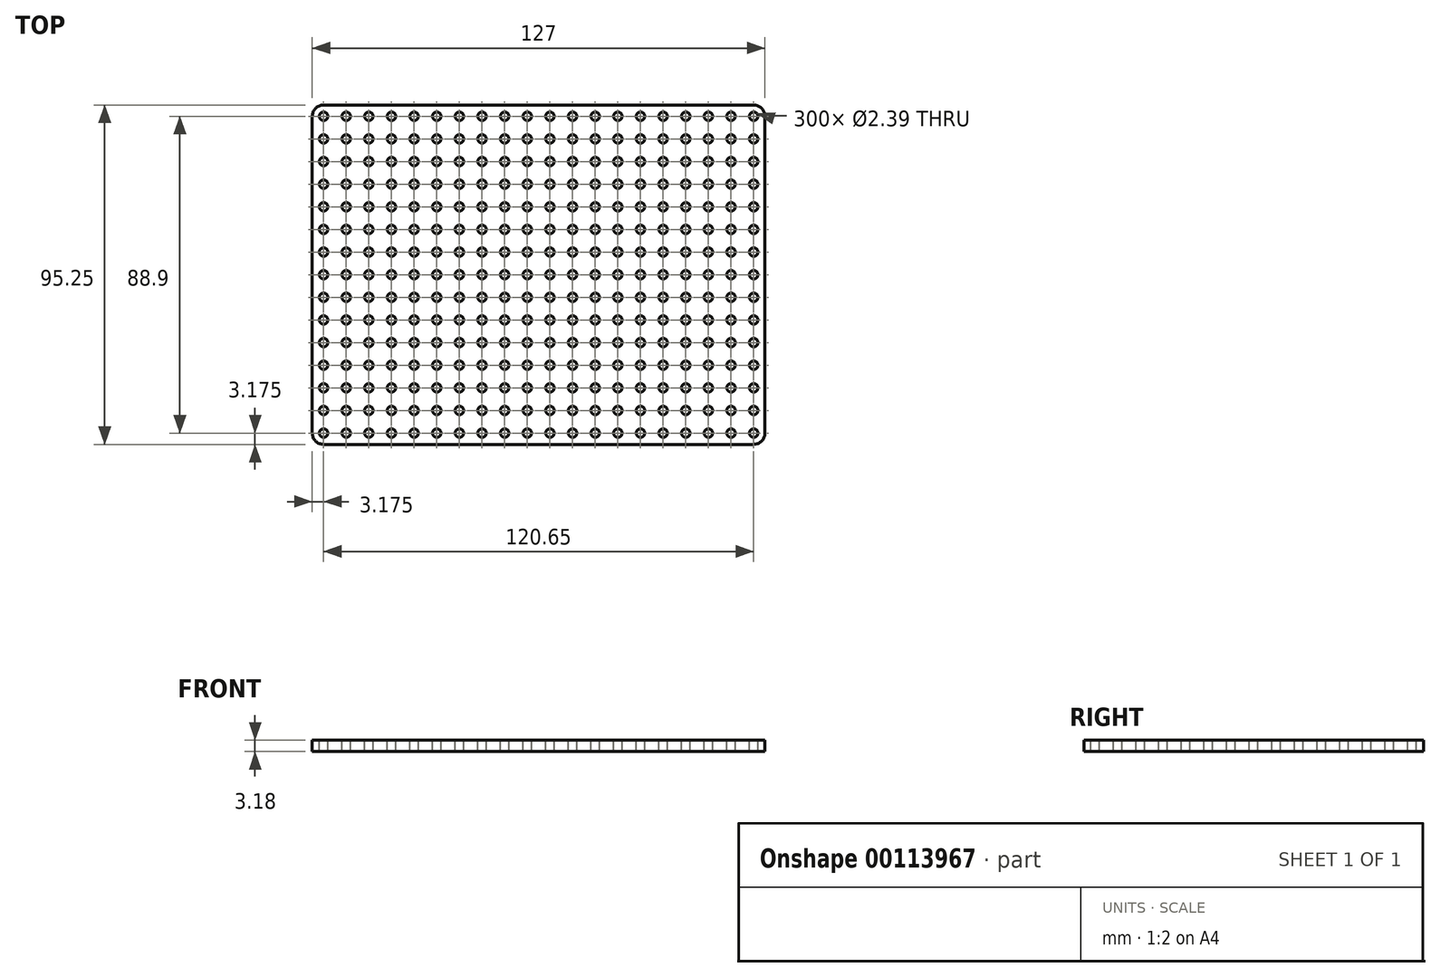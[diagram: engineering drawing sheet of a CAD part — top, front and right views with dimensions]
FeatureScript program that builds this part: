
annotation { "Feature Type Name" : "Feature", "Feature Type Description" : "" }
export const myFeature = defineFeature(function(context is Context, id is Id, definition is map)
    precondition{}
    {
        {
            var Q0;
            Q0=qCreatedBy(makeId("Top.planeOp"),FACE);
            var sketch = newSketch(context, id + "F0", { "sketchPlane" : qUnion([Q0])});
            skLineSegment(sketch, "E0.bottom", {"start": v(3.17, 0) * mm, "end": v(123.83, 0) * mm});
            skLineSegment(sketch, "E0.top", {"start": v(3.17, 95.25) * mm, "end": v(123.82, 95.25) * mm});
            skLineSegment(sketch, "E0.left", {"start": v(0, 3.17) * mm, "end": v(0, 92.08) * mm});
            skLineSegment(sketch, "E0.right", {"start": v(127, 3.17) * mm, "end": v(127, 92.08) * mm});
            skPoint(sketch, "E1.visualSharp", {"position": v(0, 95.25) * mm});
            skArc(sketch, "E1.filletArc", {"start": v(3.17, 95.25) * mm, "mid": v(0.93, 94.32) * mm, "end": v(0, 92.08) * mm});
            skPoint(sketch, "E2.visualSharp", {"position": v(127, 95.25) * mm});
            skArc(sketch, "E2.filletArc", {"start": v(127, 92.08) * mm, "mid": v(126.07, 94.32) * mm, "end": v(123.82, 95.25) * mm});
            skPoint(sketch, "E3.visualSharp", {"position": v(127, 0) * mm});
            skArc(sketch, "E3.filletArc", {"start": v(123.83, 0) * mm, "mid": v(126.07, 0.93) * mm, "end": v(127, 3.18) * mm});
            skPoint(sketch, "E4.visualSharp", {"position": v(0, 0) * mm});
            skArc(sketch, "E4.filletArc", {"start": v(0, 3.17) * mm, "mid": v(0.93, 0.93) * mm, "end": v(3.17, 0) * mm});
            skSolve(sketch);
        }
        {
            var Q0;
            Q0=qSketchRegion(id+"F0",true);
            extrude(context, id + "F1", {"entities" : qUnion([Q0]), "depth" : 3.17 * mm});
        }
        {
            var Q0;
            Q0=makeQuery(id+"F1.opExtrude","CAP_FACE",FACE,{"disambiguationData":[OSD([sQuery(id+"F0.wireOp",EDGE,"E0.bottom"),sQuery(id+"F0.wireOp",EDGE,"E0.top"),sQuery(id+"F0.wireOp",EDGE,"E0.left"),sQuery(id+"F0.wireOp",EDGE,"E0.right"),sQuery(id+"F0.wireOp",EDGE,"E1.filletArc"),sQuery(id+"F0.wireOp",EDGE,"E2.filletArc"),sQuery(id+"F0.wireOp",EDGE,"E3.filletArc"),sQuery(id+"F0.wireOp",EDGE,"E4.filletArc")])],"isStart":false});
            var sketch = newSketch(context, id + "F2", { "sketchPlane" : qUnion([Q0])});
            skCircle(sketch, "E5", {"center": v(3.18, 3.17) * mm, "radius": 1.2 * mm});
            skCircle(sketch, "E6.0.1.0", {"center": v(3.18, 9.52) * mm, "radius": 1.2 * mm});
            skCircle(sketch, "E6.0.2.0", {"center": v(3.18, 15.88) * mm, "radius": 1.2 * mm});
            skCircle(sketch, "E6.0.3.0", {"center": v(3.18, 22.23) * mm, "radius": 1.2 * mm});
            skCircle(sketch, "E6.0.4.0", {"center": v(3.18, 28.58) * mm, "radius": 1.2 * mm});
            skCircle(sketch, "E6.0.5.0", {"center": v(3.18, 34.93) * mm, "radius": 1.2 * mm});
            skCircle(sketch, "E6.0.6.0", {"center": v(3.18, 41.28) * mm, "radius": 1.2 * mm});
            skCircle(sketch, "E6.0.7.0", {"center": v(3.18, 47.63) * mm, "radius": 1.2 * mm});
            skCircle(sketch, "E6.0.8.0", {"center": v(3.18, 53.98) * mm, "radius": 1.2 * mm});
            skCircle(sketch, "E6.0.9.0", {"center": v(3.18, 60.33) * mm, "radius": 1.2 * mm});
            skCircle(sketch, "E6.0.10.0", {"center": v(3.18, 66.68) * mm, "radius": 1.2 * mm});
            skCircle(sketch, "E6.0.11.0", {"center": v(3.18, 73.03) * mm, "radius": 1.2 * mm});
            skCircle(sketch, "E6.0.12.0", {"center": v(3.18, 79.38) * mm, "radius": 1.2 * mm});
            skCircle(sketch, "E6.0.13.0", {"center": v(3.18, 85.73) * mm, "radius": 1.2 * mm});
            skCircle(sketch, "E6.0.14.0", {"center": v(3.18, 92.08) * mm, "radius": 1.2 * mm});
            skCircle(sketch, "E6.1.0.0", {"center": v(9.53, 3.17) * mm, "radius": 1.2 * mm});
            skCircle(sketch, "E6.1.1.0", {"center": v(9.53, 9.52) * mm, "radius": 1.2 * mm});
            skCircle(sketch, "E6.1.2.0", {"center": v(9.53, 15.88) * mm, "radius": 1.2 * mm});
            skCircle(sketch, "E6.1.3.0", {"center": v(9.53, 22.23) * mm, "radius": 1.2 * mm});
            skCircle(sketch, "E6.1.4.0", {"center": v(9.53, 28.58) * mm, "radius": 1.2 * mm});
            skCircle(sketch, "E6.1.5.0", {"center": v(9.53, 34.93) * mm, "radius": 1.2 * mm});
            skCircle(sketch, "E6.1.6.0", {"center": v(9.53, 41.28) * mm, "radius": 1.2 * mm});
            skCircle(sketch, "E6.1.7.0", {"center": v(9.53, 47.63) * mm, "radius": 1.2 * mm});
            skCircle(sketch, "E6.1.8.0", {"center": v(9.53, 53.98) * mm, "radius": 1.2 * mm});
            skCircle(sketch, "E6.1.9.0", {"center": v(9.53, 60.33) * mm, "radius": 1.2 * mm});
            skCircle(sketch, "E6.1.10.0", {"center": v(9.53, 66.68) * mm, "radius": 1.2 * mm});
            skCircle(sketch, "E6.1.11.0", {"center": v(9.53, 73.03) * mm, "radius": 1.2 * mm});
            skCircle(sketch, "E6.1.12.0", {"center": v(9.53, 79.38) * mm, "radius": 1.2 * mm});
            skCircle(sketch, "E6.1.13.0", {"center": v(9.53, 85.73) * mm, "radius": 1.2 * mm});
            skCircle(sketch, "E6.1.14.0", {"center": v(9.53, 92.08) * mm, "radius": 1.2 * mm});
            skCircle(sketch, "E6.2.0.0", {"center": v(15.88, 3.17) * mm, "radius": 1.2 * mm});
            skCircle(sketch, "E6.2.1.0", {"center": v(15.88, 9.52) * mm, "radius": 1.2 * mm});
            skCircle(sketch, "E6.2.2.0", {"center": v(15.88, 15.88) * mm, "radius": 1.2 * mm});
            skCircle(sketch, "E6.2.3.0", {"center": v(15.88, 22.23) * mm, "radius": 1.2 * mm});
            skCircle(sketch, "E6.2.4.0", {"center": v(15.88, 28.58) * mm, "radius": 1.2 * mm});
            skCircle(sketch, "E6.2.5.0", {"center": v(15.88, 34.93) * mm, "radius": 1.2 * mm});
            skCircle(sketch, "E6.2.6.0", {"center": v(15.88, 41.28) * mm, "radius": 1.2 * mm});
            skCircle(sketch, "E6.2.7.0", {"center": v(15.88, 47.63) * mm, "radius": 1.2 * mm});
            skCircle(sketch, "E6.2.8.0", {"center": v(15.88, 53.98) * mm, "radius": 1.2 * mm});
            skCircle(sketch, "E6.2.9.0", {"center": v(15.88, 60.33) * mm, "radius": 1.2 * mm});
            skCircle(sketch, "E6.2.10.0", {"center": v(15.88, 66.68) * mm, "radius": 1.2 * mm});
            skCircle(sketch, "E6.2.11.0", {"center": v(15.88, 73.03) * mm, "radius": 1.2 * mm});
            skCircle(sketch, "E6.2.12.0", {"center": v(15.88, 79.38) * mm, "radius": 1.2 * mm});
            skCircle(sketch, "E6.2.13.0", {"center": v(15.88, 85.73) * mm, "radius": 1.2 * mm});
            skCircle(sketch, "E6.2.14.0", {"center": v(15.88, 92.08) * mm, "radius": 1.2 * mm});
            skCircle(sketch, "E6.3.0.0", {"center": v(22.22, 3.17) * mm, "radius": 1.2 * mm});
            skCircle(sketch, "E6.3.1.0", {"center": v(22.22, 9.52) * mm, "radius": 1.2 * mm});
            skCircle(sketch, "E6.3.2.0", {"center": v(22.22, 15.88) * mm, "radius": 1.2 * mm});
            skCircle(sketch, "E6.3.3.0", {"center": v(22.22, 22.23) * mm, "radius": 1.2 * mm});
            skCircle(sketch, "E6.3.4.0", {"center": v(22.22, 28.58) * mm, "radius": 1.2 * mm});
            skCircle(sketch, "E6.3.5.0", {"center": v(22.22, 34.93) * mm, "radius": 1.2 * mm});
            skCircle(sketch, "E6.3.6.0", {"center": v(22.22, 41.28) * mm, "radius": 1.2 * mm});
            skCircle(sketch, "E6.3.7.0", {"center": v(22.22, 47.63) * mm, "radius": 1.2 * mm});
            skCircle(sketch, "E6.3.8.0", {"center": v(22.22, 53.98) * mm, "radius": 1.2 * mm});
            skCircle(sketch, "E6.3.9.0", {"center": v(22.22, 60.33) * mm, "radius": 1.2 * mm});
            skCircle(sketch, "E6.3.10.0", {"center": v(22.22, 66.68) * mm, "radius": 1.2 * mm});
            skCircle(sketch, "E6.3.11.0", {"center": v(22.22, 73.03) * mm, "radius": 1.2 * mm});
            skCircle(sketch, "E6.3.12.0", {"center": v(22.22, 79.38) * mm, "radius": 1.2 * mm});
            skCircle(sketch, "E6.3.13.0", {"center": v(22.22, 85.73) * mm, "radius": 1.2 * mm});
            skCircle(sketch, "E6.3.14.0", {"center": v(22.22, 92.08) * mm, "radius": 1.2 * mm});
            skCircle(sketch, "E6.4.0.0", {"center": v(28.57, 3.17) * mm, "radius": 1.2 * mm});
            skCircle(sketch, "E6.4.1.0", {"center": v(28.57, 9.52) * mm, "radius": 1.2 * mm});
            skCircle(sketch, "E6.4.2.0", {"center": v(28.57, 15.88) * mm, "radius": 1.2 * mm});
            skCircle(sketch, "E6.4.3.0", {"center": v(28.57, 22.23) * mm, "radius": 1.2 * mm});
            skCircle(sketch, "E6.4.4.0", {"center": v(28.57, 28.58) * mm, "radius": 1.2 * mm});
            skCircle(sketch, "E6.4.5.0", {"center": v(28.57, 34.93) * mm, "radius": 1.2 * mm});
            skCircle(sketch, "E6.4.6.0", {"center": v(28.57, 41.28) * mm, "radius": 1.2 * mm});
            skCircle(sketch, "E6.4.7.0", {"center": v(28.57, 47.63) * mm, "radius": 1.2 * mm});
            skCircle(sketch, "E6.4.8.0", {"center": v(28.57, 53.98) * mm, "radius": 1.2 * mm});
            skCircle(sketch, "E6.4.9.0", {"center": v(28.57, 60.33) * mm, "radius": 1.2 * mm});
            skCircle(sketch, "E6.4.10.0", {"center": v(28.57, 66.68) * mm, "radius": 1.2 * mm});
            skCircle(sketch, "E6.4.11.0", {"center": v(28.57, 73.03) * mm, "radius": 1.2 * mm});
            skCircle(sketch, "E6.4.12.0", {"center": v(28.57, 79.38) * mm, "radius": 1.2 * mm});
            skCircle(sketch, "E6.4.13.0", {"center": v(28.57, 85.73) * mm, "radius": 1.2 * mm});
            skCircle(sketch, "E6.4.14.0", {"center": v(28.57, 92.08) * mm, "radius": 1.2 * mm});
            skCircle(sketch, "E6.5.0.0", {"center": v(34.92, 3.17) * mm, "radius": 1.2 * mm});
            skCircle(sketch, "E6.5.1.0", {"center": v(34.92, 9.52) * mm, "radius": 1.2 * mm});
            skCircle(sketch, "E6.5.2.0", {"center": v(34.92, 15.88) * mm, "radius": 1.2 * mm});
            skCircle(sketch, "E6.5.3.0", {"center": v(34.92, 22.23) * mm, "radius": 1.2 * mm});
            skCircle(sketch, "E6.5.4.0", {"center": v(34.92, 28.58) * mm, "radius": 1.2 * mm});
            skCircle(sketch, "E6.5.5.0", {"center": v(34.92, 34.93) * mm, "radius": 1.2 * mm});
            skCircle(sketch, "E6.5.6.0", {"center": v(34.92, 41.28) * mm, "radius": 1.2 * mm});
            skCircle(sketch, "E6.5.7.0", {"center": v(34.92, 47.63) * mm, "radius": 1.2 * mm});
            skCircle(sketch, "E6.5.8.0", {"center": v(34.92, 53.98) * mm, "radius": 1.2 * mm});
            skCircle(sketch, "E6.5.9.0", {"center": v(34.92, 60.33) * mm, "radius": 1.2 * mm});
            skCircle(sketch, "E6.5.10.0", {"center": v(34.92, 66.68) * mm, "radius": 1.2 * mm});
            skCircle(sketch, "E6.5.11.0", {"center": v(34.92, 73.03) * mm, "radius": 1.2 * mm});
            skCircle(sketch, "E6.5.12.0", {"center": v(34.92, 79.38) * mm, "radius": 1.2 * mm});
            skCircle(sketch, "E6.5.13.0", {"center": v(34.92, 85.73) * mm, "radius": 1.2 * mm});
            skCircle(sketch, "E6.5.14.0", {"center": v(34.92, 92.08) * mm, "radius": 1.2 * mm});
            skCircle(sketch, "E6.6.0.0", {"center": v(41.27, 3.17) * mm, "radius": 1.2 * mm});
            skCircle(sketch, "E6.6.1.0", {"center": v(41.27, 9.52) * mm, "radius": 1.2 * mm});
            skCircle(sketch, "E6.6.2.0", {"center": v(41.27, 15.88) * mm, "radius": 1.2 * mm});
            skCircle(sketch, "E6.6.3.0", {"center": v(41.27, 22.23) * mm, "radius": 1.2 * mm});
            skCircle(sketch, "E6.6.4.0", {"center": v(41.27, 28.58) * mm, "radius": 1.2 * mm});
            skCircle(sketch, "E6.6.5.0", {"center": v(41.27, 34.93) * mm, "radius": 1.2 * mm});
            skCircle(sketch, "E6.6.6.0", {"center": v(41.27, 41.28) * mm, "radius": 1.2 * mm});
            skCircle(sketch, "E6.6.7.0", {"center": v(41.27, 47.63) * mm, "radius": 1.2 * mm});
            skCircle(sketch, "E6.6.8.0", {"center": v(41.27, 53.98) * mm, "radius": 1.2 * mm});
            skCircle(sketch, "E6.6.9.0", {"center": v(41.27, 60.33) * mm, "radius": 1.2 * mm});
            skCircle(sketch, "E6.6.10.0", {"center": v(41.27, 66.68) * mm, "radius": 1.2 * mm});
            skCircle(sketch, "E6.6.11.0", {"center": v(41.27, 73.03) * mm, "radius": 1.2 * mm});
            skCircle(sketch, "E6.6.12.0", {"center": v(41.27, 79.38) * mm, "radius": 1.2 * mm});
            skCircle(sketch, "E6.6.13.0", {"center": v(41.27, 85.73) * mm, "radius": 1.2 * mm});
            skCircle(sketch, "E6.6.14.0", {"center": v(41.27, 92.08) * mm, "radius": 1.2 * mm});
            skCircle(sketch, "E6.7.0.0", {"center": v(47.62, 3.17) * mm, "radius": 1.2 * mm});
            skCircle(sketch, "E6.7.1.0", {"center": v(47.62, 9.52) * mm, "radius": 1.2 * mm});
            skCircle(sketch, "E6.7.2.0", {"center": v(47.62, 15.88) * mm, "radius": 1.2 * mm});
            skCircle(sketch, "E6.7.3.0", {"center": v(47.62, 22.23) * mm, "radius": 1.2 * mm});
            skCircle(sketch, "E6.7.4.0", {"center": v(47.62, 28.58) * mm, "radius": 1.2 * mm});
            skCircle(sketch, "E6.7.5.0", {"center": v(47.62, 34.93) * mm, "radius": 1.2 * mm});
            skCircle(sketch, "E6.7.6.0", {"center": v(47.62, 41.28) * mm, "radius": 1.2 * mm});
            skCircle(sketch, "E6.7.7.0", {"center": v(47.62, 47.63) * mm, "radius": 1.2 * mm});
            skCircle(sketch, "E6.7.8.0", {"center": v(47.62, 53.98) * mm, "radius": 1.2 * mm});
            skCircle(sketch, "E6.7.9.0", {"center": v(47.62, 60.33) * mm, "radius": 1.2 * mm});
            skCircle(sketch, "E6.7.10.0", {"center": v(47.62, 66.68) * mm, "radius": 1.2 * mm});
            skCircle(sketch, "E6.7.11.0", {"center": v(47.62, 73.03) * mm, "radius": 1.2 * mm});
            skCircle(sketch, "E6.7.12.0", {"center": v(47.62, 79.38) * mm, "radius": 1.2 * mm});
            skCircle(sketch, "E6.7.13.0", {"center": v(47.62, 85.73) * mm, "radius": 1.2 * mm});
            skCircle(sketch, "E6.7.14.0", {"center": v(47.62, 92.08) * mm, "radius": 1.2 * mm});
            skCircle(sketch, "E6.8.0.0", {"center": v(53.97, 3.17) * mm, "radius": 1.2 * mm});
            skCircle(sketch, "E6.8.1.0", {"center": v(53.97, 9.52) * mm, "radius": 1.2 * mm});
            skCircle(sketch, "E6.8.2.0", {"center": v(53.97, 15.88) * mm, "radius": 1.2 * mm});
            skCircle(sketch, "E6.8.3.0", {"center": v(53.97, 22.23) * mm, "radius": 1.2 * mm});
            skCircle(sketch, "E6.8.4.0", {"center": v(53.97, 28.58) * mm, "radius": 1.2 * mm});
            skCircle(sketch, "E6.8.5.0", {"center": v(53.97, 34.93) * mm, "radius": 1.2 * mm});
            skCircle(sketch, "E6.8.6.0", {"center": v(53.97, 41.28) * mm, "radius": 1.2 * mm});
            skCircle(sketch, "E6.8.7.0", {"center": v(53.97, 47.63) * mm, "radius": 1.2 * mm});
            skCircle(sketch, "E6.8.8.0", {"center": v(53.97, 53.98) * mm, "radius": 1.2 * mm});
            skCircle(sketch, "E6.8.9.0", {"center": v(53.97, 60.33) * mm, "radius": 1.2 * mm});
            skCircle(sketch, "E6.8.10.0", {"center": v(53.97, 66.68) * mm, "radius": 1.2 * mm});
            skCircle(sketch, "E6.8.11.0", {"center": v(53.97, 73.03) * mm, "radius": 1.2 * mm});
            skCircle(sketch, "E6.8.12.0", {"center": v(53.97, 79.38) * mm, "radius": 1.2 * mm});
            skCircle(sketch, "E6.8.13.0", {"center": v(53.97, 85.73) * mm, "radius": 1.2 * mm});
            skCircle(sketch, "E6.8.14.0", {"center": v(53.97, 92.08) * mm, "radius": 1.2 * mm});
            skCircle(sketch, "E6.9.0.0", {"center": v(60.32, 3.17) * mm, "radius": 1.2 * mm});
            skCircle(sketch, "E6.9.1.0", {"center": v(60.32, 9.52) * mm, "radius": 1.2 * mm});
            skCircle(sketch, "E6.9.2.0", {"center": v(60.32, 15.88) * mm, "radius": 1.2 * mm});
            skCircle(sketch, "E6.9.3.0", {"center": v(60.32, 22.23) * mm, "radius": 1.2 * mm});
            skCircle(sketch, "E6.9.4.0", {"center": v(60.32, 28.58) * mm, "radius": 1.2 * mm});
            skCircle(sketch, "E6.9.5.0", {"center": v(60.32, 34.93) * mm, "radius": 1.2 * mm});
            skCircle(sketch, "E6.9.6.0", {"center": v(60.32, 41.28) * mm, "radius": 1.2 * mm});
            skCircle(sketch, "E6.9.7.0", {"center": v(60.32, 47.63) * mm, "radius": 1.2 * mm});
            skCircle(sketch, "E6.9.8.0", {"center": v(60.32, 53.98) * mm, "radius": 1.2 * mm});
            skCircle(sketch, "E6.9.9.0", {"center": v(60.32, 60.33) * mm, "radius": 1.2 * mm});
            skCircle(sketch, "E6.9.10.0", {"center": v(60.32, 66.68) * mm, "radius": 1.2 * mm});
            skCircle(sketch, "E6.9.11.0", {"center": v(60.32, 73.03) * mm, "radius": 1.2 * mm});
            skCircle(sketch, "E6.9.12.0", {"center": v(60.32, 79.38) * mm, "radius": 1.2 * mm});
            skCircle(sketch, "E6.9.13.0", {"center": v(60.32, 85.73) * mm, "radius": 1.2 * mm});
            skCircle(sketch, "E6.9.14.0", {"center": v(60.32, 92.08) * mm, "radius": 1.2 * mm});
            skCircle(sketch, "E6.10.0.0", {"center": v(66.67, 3.17) * mm, "radius": 1.2 * mm});
            skCircle(sketch, "E6.10.1.0", {"center": v(66.67, 9.52) * mm, "radius": 1.2 * mm});
            skCircle(sketch, "E6.10.2.0", {"center": v(66.67, 15.88) * mm, "radius": 1.2 * mm});
            skCircle(sketch, "E6.10.3.0", {"center": v(66.67, 22.23) * mm, "radius": 1.2 * mm});
            skCircle(sketch, "E6.10.4.0", {"center": v(66.67, 28.58) * mm, "radius": 1.2 * mm});
            skCircle(sketch, "E6.10.5.0", {"center": v(66.67, 34.93) * mm, "radius": 1.2 * mm});
            skCircle(sketch, "E6.10.6.0", {"center": v(66.67, 41.28) * mm, "radius": 1.2 * mm});
            skCircle(sketch, "E6.10.7.0", {"center": v(66.67, 47.63) * mm, "radius": 1.2 * mm});
            skCircle(sketch, "E6.10.8.0", {"center": v(66.67, 53.98) * mm, "radius": 1.2 * mm});
            skCircle(sketch, "E6.10.9.0", {"center": v(66.67, 60.33) * mm, "radius": 1.2 * mm});
            skCircle(sketch, "E6.10.10.0", {"center": v(66.67, 66.68) * mm, "radius": 1.2 * mm});
            skCircle(sketch, "E6.10.11.0", {"center": v(66.67, 73.03) * mm, "radius": 1.2 * mm});
            skCircle(sketch, "E6.10.12.0", {"center": v(66.67, 79.38) * mm, "radius": 1.2 * mm});
            skCircle(sketch, "E6.10.13.0", {"center": v(66.67, 85.73) * mm, "radius": 1.2 * mm});
            skCircle(sketch, "E6.10.14.0", {"center": v(66.67, 92.08) * mm, "radius": 1.2 * mm});
            skCircle(sketch, "E6.11.0.0", {"center": v(73.02, 3.17) * mm, "radius": 1.2 * mm});
            skCircle(sketch, "E6.11.1.0", {"center": v(73.02, 9.52) * mm, "radius": 1.2 * mm});
            skCircle(sketch, "E6.11.2.0", {"center": v(73.02, 15.88) * mm, "radius": 1.2 * mm});
            skCircle(sketch, "E6.11.3.0", {"center": v(73.02, 22.23) * mm, "radius": 1.2 * mm});
            skCircle(sketch, "E6.11.4.0", {"center": v(73.02, 28.58) * mm, "radius": 1.2 * mm});
            skCircle(sketch, "E6.11.5.0", {"center": v(73.02, 34.93) * mm, "radius": 1.2 * mm});
            skCircle(sketch, "E6.11.6.0", {"center": v(73.02, 41.28) * mm, "radius": 1.2 * mm});
            skCircle(sketch, "E6.11.7.0", {"center": v(73.02, 47.63) * mm, "radius": 1.2 * mm});
            skCircle(sketch, "E6.11.8.0", {"center": v(73.02, 53.98) * mm, "radius": 1.2 * mm});
            skCircle(sketch, "E6.11.9.0", {"center": v(73.02, 60.33) * mm, "radius": 1.2 * mm});
            skCircle(sketch, "E6.11.10.0", {"center": v(73.02, 66.68) * mm, "radius": 1.2 * mm});
            skCircle(sketch, "E6.11.11.0", {"center": v(73.02, 73.03) * mm, "radius": 1.2 * mm});
            skCircle(sketch, "E6.11.12.0", {"center": v(73.02, 79.38) * mm, "radius": 1.2 * mm});
            skCircle(sketch, "E6.11.13.0", {"center": v(73.02, 85.73) * mm, "radius": 1.2 * mm});
            skCircle(sketch, "E6.11.14.0", {"center": v(73.02, 92.08) * mm, "radius": 1.2 * mm});
            skCircle(sketch, "E6.12.0.0", {"center": v(79.37, 3.17) * mm, "radius": 1.2 * mm});
            skCircle(sketch, "E6.12.1.0", {"center": v(79.37, 9.52) * mm, "radius": 1.2 * mm});
            skCircle(sketch, "E6.12.2.0", {"center": v(79.37, 15.88) * mm, "radius": 1.2 * mm});
            skCircle(sketch, "E6.12.3.0", {"center": v(79.37, 22.23) * mm, "radius": 1.2 * mm});
            skCircle(sketch, "E6.12.4.0", {"center": v(79.37, 28.58) * mm, "radius": 1.2 * mm});
            skCircle(sketch, "E6.12.5.0", {"center": v(79.37, 34.93) * mm, "radius": 1.2 * mm});
            skCircle(sketch, "E6.12.6.0", {"center": v(79.37, 41.28) * mm, "radius": 1.2 * mm});
            skCircle(sketch, "E6.12.7.0", {"center": v(79.37, 47.63) * mm, "radius": 1.2 * mm});
            skCircle(sketch, "E6.12.8.0", {"center": v(79.37, 53.98) * mm, "radius": 1.2 * mm});
            skCircle(sketch, "E6.12.9.0", {"center": v(79.37, 60.33) * mm, "radius": 1.2 * mm});
            skCircle(sketch, "E6.12.10.0", {"center": v(79.37, 66.68) * mm, "radius": 1.2 * mm});
            skCircle(sketch, "E6.12.11.0", {"center": v(79.37, 73.03) * mm, "radius": 1.2 * mm});
            skCircle(sketch, "E6.12.12.0", {"center": v(79.37, 79.38) * mm, "radius": 1.2 * mm});
            skCircle(sketch, "E6.12.13.0", {"center": v(79.37, 85.73) * mm, "radius": 1.2 * mm});
            skCircle(sketch, "E6.12.14.0", {"center": v(79.37, 92.08) * mm, "radius": 1.2 * mm});
            skCircle(sketch, "E6.13.0.0", {"center": v(85.72, 3.17) * mm, "radius": 1.2 * mm});
            skCircle(sketch, "E6.13.1.0", {"center": v(85.72, 9.52) * mm, "radius": 1.2 * mm});
            skCircle(sketch, "E6.13.2.0", {"center": v(85.72, 15.88) * mm, "radius": 1.2 * mm});
            skCircle(sketch, "E6.13.3.0", {"center": v(85.72, 22.23) * mm, "radius": 1.2 * mm});
            skCircle(sketch, "E6.13.4.0", {"center": v(85.72, 28.58) * mm, "radius": 1.2 * mm});
            skCircle(sketch, "E6.13.5.0", {"center": v(85.72, 34.93) * mm, "radius": 1.2 * mm});
            skCircle(sketch, "E6.13.6.0", {"center": v(85.72, 41.28) * mm, "radius": 1.2 * mm});
            skCircle(sketch, "E6.13.7.0", {"center": v(85.72, 47.63) * mm, "radius": 1.2 * mm});
            skCircle(sketch, "E6.13.8.0", {"center": v(85.72, 53.98) * mm, "radius": 1.2 * mm});
            skCircle(sketch, "E6.13.9.0", {"center": v(85.72, 60.33) * mm, "radius": 1.2 * mm});
            skCircle(sketch, "E6.13.10.0", {"center": v(85.72, 66.68) * mm, "radius": 1.2 * mm});
            skCircle(sketch, "E6.13.11.0", {"center": v(85.72, 73.03) * mm, "radius": 1.2 * mm});
            skCircle(sketch, "E6.13.12.0", {"center": v(85.72, 79.38) * mm, "radius": 1.2 * mm});
            skCircle(sketch, "E6.13.13.0", {"center": v(85.72, 85.73) * mm, "radius": 1.2 * mm});
            skCircle(sketch, "E6.13.14.0", {"center": v(85.72, 92.08) * mm, "radius": 1.2 * mm});
            skCircle(sketch, "E6.14.0.0", {"center": v(92.07, 3.17) * mm, "radius": 1.2 * mm});
            skCircle(sketch, "E6.14.1.0", {"center": v(92.07, 9.52) * mm, "radius": 1.2 * mm});
            skCircle(sketch, "E6.14.2.0", {"center": v(92.07, 15.88) * mm, "radius": 1.2 * mm});
            skCircle(sketch, "E6.14.3.0", {"center": v(92.07, 22.23) * mm, "radius": 1.2 * mm});
            skCircle(sketch, "E6.14.4.0", {"center": v(92.07, 28.58) * mm, "radius": 1.2 * mm});
            skCircle(sketch, "E6.14.5.0", {"center": v(92.07, 34.93) * mm, "radius": 1.2 * mm});
            skCircle(sketch, "E6.14.6.0", {"center": v(92.07, 41.28) * mm, "radius": 1.2 * mm});
            skCircle(sketch, "E6.14.7.0", {"center": v(92.07, 47.63) * mm, "radius": 1.2 * mm});
            skCircle(sketch, "E6.14.8.0", {"center": v(92.07, 53.98) * mm, "radius": 1.2 * mm});
            skCircle(sketch, "E6.14.9.0", {"center": v(92.07, 60.33) * mm, "radius": 1.2 * mm});
            skCircle(sketch, "E6.14.10.0", {"center": v(92.07, 66.68) * mm, "radius": 1.2 * mm});
            skCircle(sketch, "E6.14.11.0", {"center": v(92.07, 73.03) * mm, "radius": 1.2 * mm});
            skCircle(sketch, "E6.14.12.0", {"center": v(92.07, 79.38) * mm, "radius": 1.2 * mm});
            skCircle(sketch, "E6.14.13.0", {"center": v(92.07, 85.73) * mm, "radius": 1.2 * mm});
            skCircle(sketch, "E6.14.14.0", {"center": v(92.07, 92.08) * mm, "radius": 1.2 * mm});
            skCircle(sketch, "E6.15.0.0", {"center": v(98.42, 3.17) * mm, "radius": 1.2 * mm});
            skCircle(sketch, "E6.15.1.0", {"center": v(98.42, 9.52) * mm, "radius": 1.2 * mm});
            skCircle(sketch, "E6.15.2.0", {"center": v(98.42, 15.88) * mm, "radius": 1.2 * mm});
            skCircle(sketch, "E6.15.3.0", {"center": v(98.42, 22.23) * mm, "radius": 1.2 * mm});
            skCircle(sketch, "E6.15.4.0", {"center": v(98.42, 28.58) * mm, "radius": 1.2 * mm});
            skCircle(sketch, "E6.15.5.0", {"center": v(98.42, 34.93) * mm, "radius": 1.2 * mm});
            skCircle(sketch, "E6.15.6.0", {"center": v(98.42, 41.28) * mm, "radius": 1.2 * mm});
            skCircle(sketch, "E6.15.7.0", {"center": v(98.42, 47.63) * mm, "radius": 1.2 * mm});
            skCircle(sketch, "E6.15.8.0", {"center": v(98.42, 53.98) * mm, "radius": 1.2 * mm});
            skCircle(sketch, "E6.15.9.0", {"center": v(98.42, 60.33) * mm, "radius": 1.2 * mm});
            skCircle(sketch, "E6.15.10.0", {"center": v(98.42, 66.68) * mm, "radius": 1.2 * mm});
            skCircle(sketch, "E6.15.11.0", {"center": v(98.42, 73.03) * mm, "radius": 1.2 * mm});
            skCircle(sketch, "E6.15.12.0", {"center": v(98.42, 79.38) * mm, "radius": 1.2 * mm});
            skCircle(sketch, "E6.15.13.0", {"center": v(98.42, 85.73) * mm, "radius": 1.2 * mm});
            skCircle(sketch, "E6.15.14.0", {"center": v(98.42, 92.08) * mm, "radius": 1.2 * mm});
            skCircle(sketch, "E6.16.0.0", {"center": v(104.77, 3.17) * mm, "radius": 1.2 * mm});
            skCircle(sketch, "E6.16.1.0", {"center": v(104.77, 9.52) * mm, "radius": 1.2 * mm});
            skCircle(sketch, "E6.16.2.0", {"center": v(104.77, 15.88) * mm, "radius": 1.2 * mm});
            skCircle(sketch, "E6.16.3.0", {"center": v(104.77, 22.23) * mm, "radius": 1.2 * mm});
            skCircle(sketch, "E6.16.4.0", {"center": v(104.77, 28.58) * mm, "radius": 1.2 * mm});
            skCircle(sketch, "E6.16.5.0", {"center": v(104.77, 34.93) * mm, "radius": 1.2 * mm});
            skCircle(sketch, "E6.16.6.0", {"center": v(104.77, 41.28) * mm, "radius": 1.2 * mm});
            skCircle(sketch, "E6.16.7.0", {"center": v(104.77, 47.63) * mm, "radius": 1.2 * mm});
            skCircle(sketch, "E6.16.8.0", {"center": v(104.77, 53.98) * mm, "radius": 1.2 * mm});
            skCircle(sketch, "E6.16.9.0", {"center": v(104.77, 60.33) * mm, "radius": 1.2 * mm});
            skCircle(sketch, "E6.16.10.0", {"center": v(104.77, 66.68) * mm, "radius": 1.2 * mm});
            skCircle(sketch, "E6.16.11.0", {"center": v(104.77, 73.03) * mm, "radius": 1.2 * mm});
            skCircle(sketch, "E6.16.12.0", {"center": v(104.77, 79.38) * mm, "radius": 1.2 * mm});
            skCircle(sketch, "E6.16.13.0", {"center": v(104.77, 85.73) * mm, "radius": 1.2 * mm});
            skCircle(sketch, "E6.16.14.0", {"center": v(104.77, 92.08) * mm, "radius": 1.2 * mm});
            skCircle(sketch, "E6.17.0.0", {"center": v(111.12, 3.17) * mm, "radius": 1.2 * mm});
            skCircle(sketch, "E6.17.1.0", {"center": v(111.12, 9.52) * mm, "radius": 1.2 * mm});
            skCircle(sketch, "E6.17.2.0", {"center": v(111.12, 15.88) * mm, "radius": 1.2 * mm});
            skCircle(sketch, "E6.17.3.0", {"center": v(111.12, 22.23) * mm, "radius": 1.2 * mm});
            skCircle(sketch, "E6.17.4.0", {"center": v(111.12, 28.58) * mm, "radius": 1.2 * mm});
            skCircle(sketch, "E6.17.5.0", {"center": v(111.12, 34.93) * mm, "radius": 1.2 * mm});
            skCircle(sketch, "E6.17.6.0", {"center": v(111.12, 41.28) * mm, "radius": 1.2 * mm});
            skCircle(sketch, "E6.17.7.0", {"center": v(111.12, 47.63) * mm, "radius": 1.2 * mm});
            skCircle(sketch, "E6.17.8.0", {"center": v(111.12, 53.98) * mm, "radius": 1.2 * mm});
            skCircle(sketch, "E6.17.9.0", {"center": v(111.12, 60.33) * mm, "radius": 1.2 * mm});
            skCircle(sketch, "E6.17.10.0", {"center": v(111.12, 66.68) * mm, "radius": 1.2 * mm});
            skCircle(sketch, "E6.17.11.0", {"center": v(111.12, 73.03) * mm, "radius": 1.2 * mm});
            skCircle(sketch, "E6.17.12.0", {"center": v(111.12, 79.38) * mm, "radius": 1.2 * mm});
            skCircle(sketch, "E6.17.13.0", {"center": v(111.12, 85.73) * mm, "radius": 1.2 * mm});
            skCircle(sketch, "E6.17.14.0", {"center": v(111.12, 92.08) * mm, "radius": 1.2 * mm});
            skCircle(sketch, "E6.18.0.0", {"center": v(117.47, 3.17) * mm, "radius": 1.2 * mm});
            skCircle(sketch, "E6.18.1.0", {"center": v(117.47, 9.52) * mm, "radius": 1.2 * mm});
            skCircle(sketch, "E6.18.2.0", {"center": v(117.47, 15.88) * mm, "radius": 1.2 * mm});
            skCircle(sketch, "E6.18.3.0", {"center": v(117.47, 22.23) * mm, "radius": 1.2 * mm});
            skCircle(sketch, "E6.18.4.0", {"center": v(117.47, 28.58) * mm, "radius": 1.2 * mm});
            skCircle(sketch, "E6.18.5.0", {"center": v(117.47, 34.93) * mm, "radius": 1.2 * mm});
            skCircle(sketch, "E6.18.6.0", {"center": v(117.47, 41.28) * mm, "radius": 1.2 * mm});
            skCircle(sketch, "E6.18.7.0", {"center": v(117.47, 47.63) * mm, "radius": 1.2 * mm});
            skCircle(sketch, "E6.18.8.0", {"center": v(117.47, 53.98) * mm, "radius": 1.2 * mm});
            skCircle(sketch, "E6.18.9.0", {"center": v(117.47, 60.33) * mm, "radius": 1.2 * mm});
            skCircle(sketch, "E6.18.10.0", {"center": v(117.47, 66.68) * mm, "radius": 1.2 * mm});
            skCircle(sketch, "E6.18.11.0", {"center": v(117.47, 73.03) * mm, "radius": 1.2 * mm});
            skCircle(sketch, "E6.18.12.0", {"center": v(117.47, 79.38) * mm, "radius": 1.2 * mm});
            skCircle(sketch, "E6.18.13.0", {"center": v(117.47, 85.73) * mm, "radius": 1.2 * mm});
            skCircle(sketch, "E6.18.14.0", {"center": v(117.47, 92.08) * mm, "radius": 1.2 * mm});
            skCircle(sketch, "E6.19.0.0", {"center": v(123.82, 3.17) * mm, "radius": 1.2 * mm});
            skCircle(sketch, "E6.19.1.0", {"center": v(123.82, 9.52) * mm, "radius": 1.2 * mm});
            skCircle(sketch, "E6.19.2.0", {"center": v(123.82, 15.88) * mm, "radius": 1.2 * mm});
            skCircle(sketch, "E6.19.3.0", {"center": v(123.82, 22.23) * mm, "radius": 1.2 * mm});
            skCircle(sketch, "E6.19.4.0", {"center": v(123.82, 28.58) * mm, "radius": 1.2 * mm});
            skCircle(sketch, "E6.19.5.0", {"center": v(123.82, 34.93) * mm, "radius": 1.2 * mm});
            skCircle(sketch, "E6.19.6.0", {"center": v(123.82, 41.28) * mm, "radius": 1.2 * mm});
            skCircle(sketch, "E6.19.7.0", {"center": v(123.82, 47.63) * mm, "radius": 1.2 * mm});
            skCircle(sketch, "E6.19.8.0", {"center": v(123.82, 53.98) * mm, "radius": 1.2 * mm});
            skCircle(sketch, "E6.19.9.0", {"center": v(123.82, 60.33) * mm, "radius": 1.2 * mm});
            skCircle(sketch, "E6.19.10.0", {"center": v(123.82, 66.68) * mm, "radius": 1.2 * mm});
            skCircle(sketch, "E6.19.11.0", {"center": v(123.82, 73.03) * mm, "radius": 1.2 * mm});
            skCircle(sketch, "E6.19.12.0", {"center": v(123.82, 79.38) * mm, "radius": 1.2 * mm});
            skCircle(sketch, "E6.19.13.0", {"center": v(123.82, 85.73) * mm, "radius": 1.2 * mm});
            skCircle(sketch, "E6.19.14.0", {"center": v(123.82, 92.08) * mm, "radius": 1.2 * mm});
            skLineSegment(sketch, "E6.direction1", {"start": v(3.18, 3.17) * mm, "end": v(9.53, 3.17) * mm, "construction": true});
            skLineSegment(sketch, "E6.direction2", {"start": v(3.18, 3.17) * mm, "end": v(3.18, 9.52) * mm, "construction": true});
            skSolve(sketch);
        }
        {
            var Q0;
            Q0 = qSketchRegion(id + "F2", true);
            extrude(context, id + "F3", {"entities" : qUnion([Q0]), "operationType" : NewBodyOperationType.REMOVE, "endBound" : BoundingType.THROUGH_ALL, "oppositeDirection" : true, "depth" : 25.4 * mm});
        }
    });
